# Revit family: Indoor_Pendant Lamp_Santa&Cole_Cirio Chandelier
name_source: partatom
category: Luminarias
revit_build: Autodesk Revit 2018 (Build: 20190510_1515(x64)
units: mm (PartAtom-declared; Revit-internal decimal feet)

## family parameters
Anfitrión = Cara
Compartido = No
Corte con vacíos al cargar = No
Cota de conector redondo = Diámetro de uso
Origen de luz = No
Punto de cálculo de habitación = No
Tipo de pieza = Normal

## types (3) — shared parameters
Assembly Instructions - CE = https://www.santacole.com
Assembly Instructions - UL = https://www.santacole.com
Elevación por defecto = 1219 mm
Energy Label = https://www.santacole.com
Fabricante = Santa & Cole
Manufacturer website = http://www.santacole.com
Modelo = Cirio Chandelier
Technical Information = https://www.santacole.com
URL = https://www.santacole.com

## per-type parameters (varying)
| type | Base M y S | Carga aparente | Cirio Chandelier L | Cirio Chandelier M | Cirio Chandelier S | Code | Load |
| Cirio Chandelier S | Sí | 114 W | No | No | Sí | CIC2x+CIPxx
CIC2x+CIPxx
CIC2x+CIPxx | 114 W |
| Cirio Chandelier M | Sí | 171 W | No | Sí | No | CIC3x+CIPxx | 171 W |
| Cirio Chandelier L | No | 228 W | Sí | No | No | CIC4x+CIPxx | 228 W |

## geometry (parser evidence)
native form markers: Sweep x9
no freeform markers — native parametric forms only
